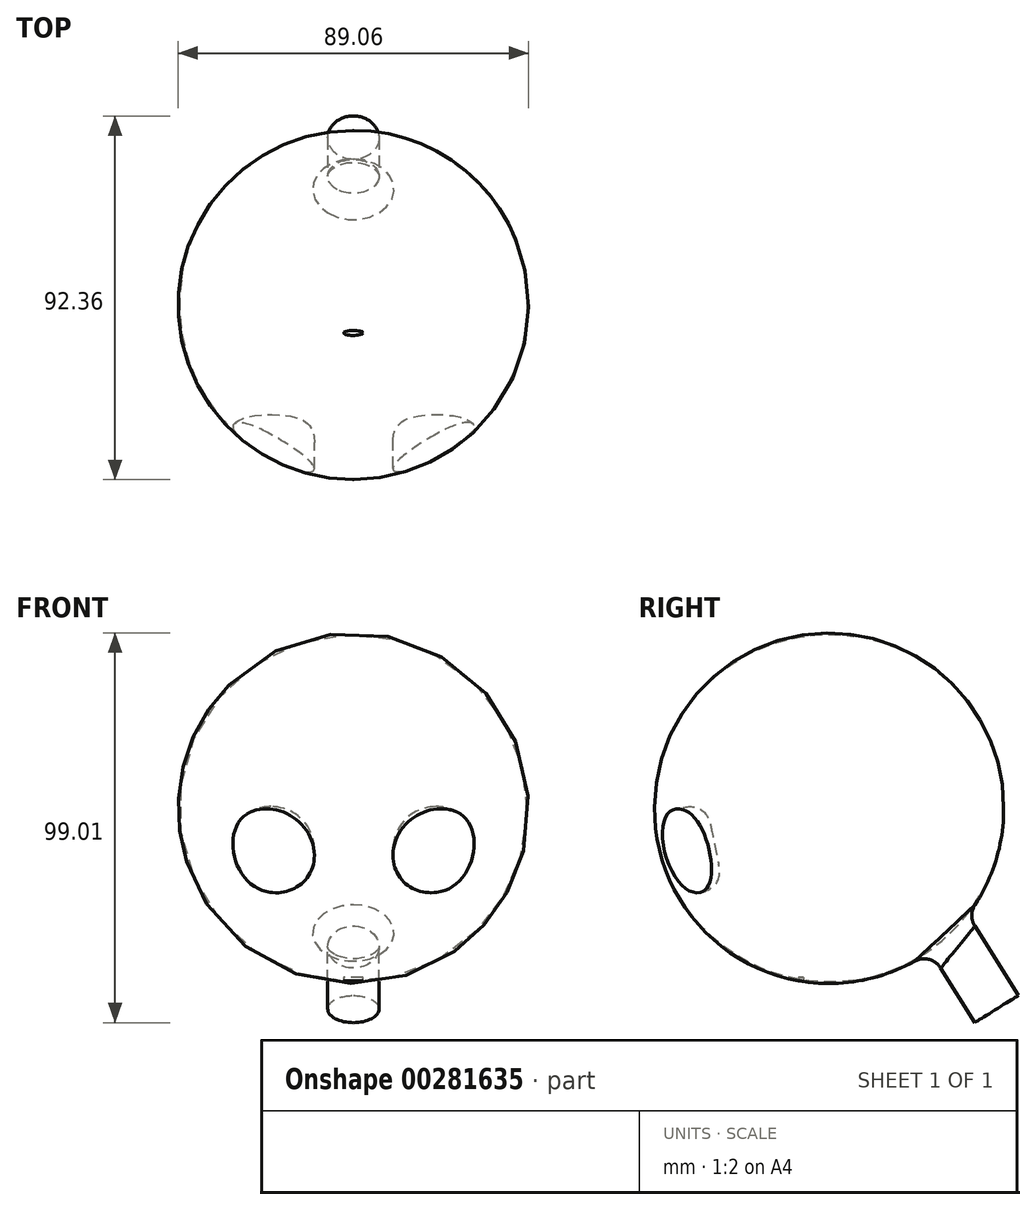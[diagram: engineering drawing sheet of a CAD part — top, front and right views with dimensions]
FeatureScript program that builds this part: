
annotation { "Feature Type Name" : "Feature", "Feature Type Description" : "" }
export const myFeature = defineFeature(function(context is Context, id is Id, definition is map)
    precondition{}
    {
        {
            var Q0;
            Q0=qCreatedBy(makeId("Top.planeOp"),FACE);
            var sketch = newSketch(context, id + "F0", { "sketchPlane" : qUnion([Q0])});
            skLineSegment(sketch, "E0", {"start": v(0, 0) * mm, "end": v(0, -88.68) * mm});
            skArc(sketch, "E1", {"start": v(0, -88.68) * mm, "mid": v(44.53, -44.34) * mm, "end": v(0, 0) * mm});
            skSolve(sketch);
        }
        {
            var Q0;
            Q0=makeQuery(id+"F0.imprint","IMPRINT",FACE,{"disambiguationData":[TD([[makeQuery(id+"F0.imprint","IMPRINT",EDGE,{"derivedFrom":sQuery(id+"F0.wireOp",EDGE,"E0")}),1.0]])]});
            var Q1;
            Q1=sQuery(id+"F0.wireOp",EDGE,"E0");
            revolve(context, id + "F1", {"surfaceOperationType" : NewSurfaceOperationType.NEW, "entities" : qUnion([Q0]), "axis" : qUnion([Q1]), "revolveType" : RevolveType.FULL});
        }
        {
            var Q0;
            Q0=qCreatedBy(makeId("Right.planeOp"),FACE);
            var sketch = newSketch(context, id + "F2", { "sketchPlane" : qUnion([Q0])});
            skLineSegment(sketch, "E2", {"start": v(-82.1, 32.84) * mm, "end": v(-64.5, -52.68) * mm});
            skLineSegment(sketch, "E3", {"start": v(0, -20.43) * mm, "end": v(-53.22, -53.63) * mm});
            skSolve(sketch);
        }
        {
            var Q0;
            Q0=sQuery(id+"F2.wireOp",EDGE,"E2");
            cPlane(context, id + "F3", {"entities" : qUnion([Q0]), "cplaneType" : CPlaneType.LINE_ANGLE, "offset" : 25 * mm, "angle" : 90 * degree, "width" : 150 * mm, "height" : 150 * mm});
        }
        {
            var Q0;
            Q0=qCreatedBy(id+"F3.planeOp",FACE);
            var sketch = newSketch(context, id + "F4", { "sketchPlane" : qUnion([Q0])});
            skCircle(sketch, "E4", {"center": v(20.9, 5.6) * mm, "radius": 11 * mm});
            skCircle(sketch, "E5", {"center": v(-21.05, 5.6) * mm, "radius": 11 * mm});
            skSolve(sketch);
        }
        {
            var Q0;
            Q0 = qSketchRegion(id + "F4", true);
            extrude(context, id + "F5", {"entities" : qUnion([Q0]), "operationType" : NewBodyOperationType.REMOVE, "oppositeDirection" : true, "depth" : 20 * mm, "offsetDistance" : 25 * mm});
        }
        {
            var Q0;
            Q0=makeQuery(id+"F5.boolean.opBoolean","COPY",EDGE,{"derivedFrom":makeQuery(id+"F5.opExtrude","CAP_EDGE",EDGE,{"disambiguationData":[OSD([sQuery(id+"F4.wireOp",EDGE,"E5")])],"isStart":true})});
            fillet(context, id + "F6", {"entities" : qUnion([Q0]), "tangentPropagation" : true, "crossSection" : FilletCrossSection.CURVATURE, "radius" : 6 * mm, "magnitude" : 0.5, "defaultsChanged" : false, "vertexSettings" : []});
        }
        {
            var Q0;
            Q0=makeQuery(id+"F5.boolean.opBoolean","COPY",EDGE,{"derivedFrom":makeQuery(id+"F5.opExtrude","CAP_EDGE",EDGE,{"disambiguationData":[OSD([sQuery(id+"F4.wireOp",EDGE,"E4")])],"isStart":true})});
            fillet(context, id + "F7", {"entities" : qUnion([Q0]), "tangentPropagation" : true, "crossSection" : FilletCrossSection.CURVATURE, "radius" : 6 * mm, "magnitude" : 0.5, "defaultsChanged" : false, "vertexSettings" : []});
        }
        {
            var Q0;
            Q0=qCreatedBy(makeId("Top.planeOp"),FACE);
            cPlane(context, id + "F8", {"entities" : qUnion([Q0]), "cplaneType" : CPlaneType.OFFSET, "offset" : 43 * mm, "oppositeDirection" : true, "width" : 150 * mm, "height" : 150 * mm});
        }
        {
            var Q0;
            Q0=qCreatedBy(id+"F8.planeOp",FACE);
            var sketch = newSketch(context, id + "F9", { "sketchPlane" : qUnion([Q0])});
            skEllipse(sketch, "E6", {"center": v(0, -51.46) * mm, "majorRadius": 2.45 * mm, "minorRadius": 0.62 * mm, "majorAxis": v(1, 0)});
            skSolve(sketch);
        }
        {
            var Q0;
            Q0 = qSketchRegion(id + "F9", true);
            extrude(context, id + "F10", {"entities" : qUnion([Q0]), "operationType" : NewBodyOperationType.REMOVE, "oppositeDirection" : true, "depth" : 25 * mm, "offsetDistance" : 25 * mm});
        }
        {
            var Q0;
            Q0=sQuery(id+"F2.wireOp",EDGE,"E3");
            cPlane(context, id + "F11", {"entities" : qUnion([Q0]), "cplaneType" : CPlaneType.LINE_ANGLE, "offset" : 25 * mm, "angle" : 0 * degree, "width" : 150 * mm, "height" : 150 * mm});
        }
        {
            var Q0;
            Q0=qCreatedBy(id+"F11.planeOp",FACE);
            var sketch = newSketch(context, id + "F12", { "sketchPlane" : qUnion([Q0])});
            skCircle(sketch, "E7", {"center": v(0, 28.57) * mm, "radius": 6.5 * mm});
            skSolve(sketch);
        }
        {
            var Q0;
            Q0=makeQuery(id+"F12.imprint","IMPRINT",FACE,{"disambiguationData":[TD([[makeQuery(id+"F12.imprint","IMPRINT",EDGE,{"derivedFrom":sQuery(id+"F12.wireOp",EDGE,"E7")}),1.0]])]});
            extrude(context, id + "F13", {"entities" : qUnion([Q0]), "operationType" : NewBodyOperationType.ADD, "depth" : 25 * mm, "offsetDistance" : 25 * mm});
        }
        {
            var Q0;
            Q0=makeQuery(id+"F13.boolean.opBoolean","INTERSECT",EDGE,{"derivedFrom":[makeQuery(id+"F1.opRevolve","SWEPT_FACE",FACE,{"disambiguationData":[OSD([sQuery(id+"F0.wireOp",EDGE,"E1")])]}),makeQuery(id+"F13.opExtrude","SWEPT_FACE",FACE,{"disambiguationData":[OSD([sQuery(id+"F12.wireOp",EDGE,"E7")])]})]});
            fillet(context, id + "F14", {"entities" : qUnion([Q0]), "tangentPropagation" : true, "radius" : 5 * mm, "defaultsChanged" : false, "vertexSettings" : []});
        }
    });
